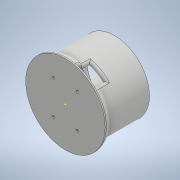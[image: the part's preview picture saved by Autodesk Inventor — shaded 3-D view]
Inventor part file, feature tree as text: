
AUTODESK INVENTOR PART (.ipt)
format: ipt  version: 2021 (Build 250183000, 183)  size: 647,168 bytes
history: native  units: mm
features: sketch x21, extrude x18, fillet x3, other x1, chamfer x1
ambient origin geometry x8: Origin, YZ Plane, XZ Plane, XY Plane, X Axis, Y Axis, Z Axis, Center Point
bodies: Body1 (feature_tree)
feature tree (44):
  other  "Sólido1"
  extrude  "Extrusión1"  Depth=144.0mm
  extrude  "Extrusión2"  Depth=100.0mm TaperAngle=0.0deg
  extrude  "Extrusión3"  Depth=124.0mm
  extrude  "Extrusión4"  Depth=104.0mm
  fillet  "Empalme1"  Radius=124.0mm
  extrude  "Extrusión5"  Depth=164.0mm
  extrude  "Extrusión6"  Depth=15.0mm TaperAngle=0.0deg
  extrude  "Extrusión7"  Depth=124.0mm
  extrude  "Extrusión8"  Depth=10.0mm TaperAngle=0.0deg
  extrude  "Extrusión9"  Depth=17.5mm TaperAngle=0.0deg
  extrude  "Extrusión10"  Depth=10.0mm TaperAngle=0.0deg
  extrude  "Extrusión11"  Depth=24.0mm
  extrude  "Extrusión12"  Depth=22.0mm
  extrude  "Extrusión13"  Depth=18.25mm TaperAngle=0.0deg
  extrude  "Extrusión14"  Depth=2.0mm TaperAngle=0.0deg
  sketch  "Boceto20"  dims[d54=2.0mm d55=0.0mm d56=5.0mm]
  sketch  "Boceto21"  dims[d57=6.0mm d58=2.0mm d59=45.0deg d72=10.0mm d73=0.0mm]
  extrude  "Extrusión15"  Depth=5.0mm
  sketch  "Boceto23"  dims[d99=120.0mm d101=360.0deg d103=1.0mm]
  extrude  "Extrusión16"  Depth=10.0mm TaperAngle=0.0deg
  extrude  "Extrusión17"  Depth=1.0mm
  fillet  "Empalme2"  Radius=4.0mm
  chamfer  "Chaflán1"  Distance=2.5mm
  extrude  "Extrusión18"  Depth=1.0mm
  fillet  "Empalme3"  [1 undecoded]
  sketch  "Boceto1"  dims[d5=124.0mm d6=144.0mm]
  sketch  "Boceto5"  dims[d7=104.0mm d8=100.0mm d9=0.0mm]
  sketch  "Boceto6"  dims[d11=104.0mm d12=124.0mm]
  sketch  "Boceto7"  dims[d13=95.0mm d14=0.0mm d15=104.0mm d16=124.0mm]
  sketch  "Boceto8"  dims[d17=80.0mm d18=0.0mm d19=164.0mm]
  sketch  "Boceto9"  dims[d20=144.0mm d21=15.0mm d22=0.0mm]
  sketch  "Boceto10"  dims[d23=15.0mm d25=124.0mm]
  sketch  "Boceto11"  dims[d26=30.0mm d27=0.0mm d30=10.0mm d31=0.0mm]
  sketch  "Boceto14"  dims[d32=8.0mm d33=0.0mm d34=17.5mm d35=0.0mm]
  sketch  "Boceto15"  dims[d36=10.0mm d37=0.0mm d38=67.25mm d39=0.0mm]
  sketch  "Boceto16"  dims[d40=64.5mm d41=0.0mm d42=24.0mm]
  sketch  "Boceto17"  dims[d43=65.0mm d44=0.0mm d45=22.0mm]
  sketch  "Boceto18"  dims[d46=2.0mm d47=0.0mm d48=18.25mm d49=0.0mm]
  sketch  "Boceto19"  dims[d50=2.0mm d51=0.0mm d52=2.0mm d53=0.0mm]
  sketch  "Boceto22"  dims[d74=1.0mm d86=4.0mm d87=4.0mm d92=2.5mm d93=6.0mm]
  sketch  "Boceto24"
  sketch  "Boceto25"
  sketch  "Boceto26"
note: 1 required parameter value undecoded (feature->parameter linkage not recoverable at this tier; creation-order binding heuristic only, values carry confidence <= 0.55)
